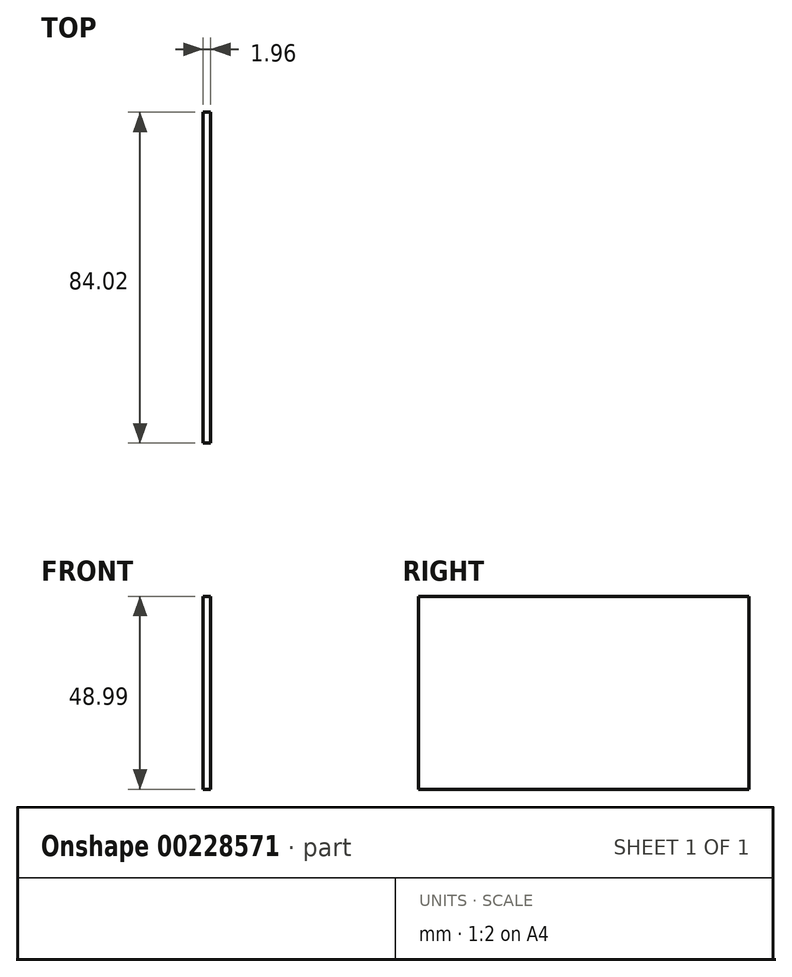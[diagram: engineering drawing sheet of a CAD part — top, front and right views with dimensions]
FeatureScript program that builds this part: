
annotation { "Feature Type Name" : "Feature", "Feature Type Description" : "" }
export const myFeature = defineFeature(function(context is Context, id is Id, definition is map)
    precondition{}
    {
        {
            var Q0;
            Q0=qCreatedBy(makeId("Right.planeOp"),FACE);
            var sketch = newSketch(context, id + "F0", { "sketchPlane" : qUnion([Q0])});
            skLineSegment(sketch, "E0.bottom", {"start": v(0, 0) * mm, "end": v(84.02, 0) * mm});
            skLineSegment(sketch, "E0.top", {"start": v(0, 49) * mm, "end": v(84.02, 49) * mm});
            skLineSegment(sketch, "E0.left", {"start": v(0, 0) * mm, "end": v(0, 49) * mm});
            skLineSegment(sketch, "E0.right", {"start": v(84.02, 0) * mm, "end": v(84.02, 49) * mm});
            skSolve(sketch);
        }
        {
            var Q0;
            Q0=makeQuery(id+"F0.imprint","IMPRINT",FACE,{"disambiguationData":[TD([[makeQuery(id+"F0.imprint","IMPRINT",EDGE,{"derivedFrom":sQuery(id+"F0.wireOp",EDGE,"E0.bottom")}),1.0]])]});
            extrude(context, id + "F1", {"entities" : qUnion([Q0]), "depth" : 1.96 * mm});
        }
    });
